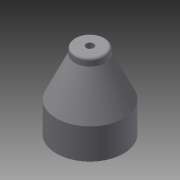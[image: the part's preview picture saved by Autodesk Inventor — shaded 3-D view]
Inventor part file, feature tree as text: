
AUTODESK INVENTOR PART (.ipt)
format: ipt  version: 2013 SP2 (Build 170200200, 200)  size: 122,880 bytes
history: native  units: mm
features: revolve x2, fillet x1, sketch x1
ambient origin geometry x8: Origin, YZ Plane, XZ Plane, XY Plane, X Axis, Y Axis, Z Axis, Center Point
bodies: Solid1 (feature_tree)
feature tree (4):
  revolve  "Revolution1"  [1 undecoded]
  revolve  "Revolution2"  Angle=90.0deg
  fillet  "Fillet1"  Radius=3.0mm
  sketch  "Sketch2"  dims[d0=2.5mm d5=4.5mm d7=90.0deg d8=3.0mm d9=90.0deg d11=9.0mm d12=16.0mm d13=20.071286mm d14=3.2mm d18=1.501155mm d19=8.149126mm d20=7.0mm d21=4.0mm d22=0.8mm d23=0.5mm]
note: 1 required parameter value undecoded (feature->parameter linkage not recoverable at this tier; creation-order binding heuristic only, values carry confidence <= 0.55)
